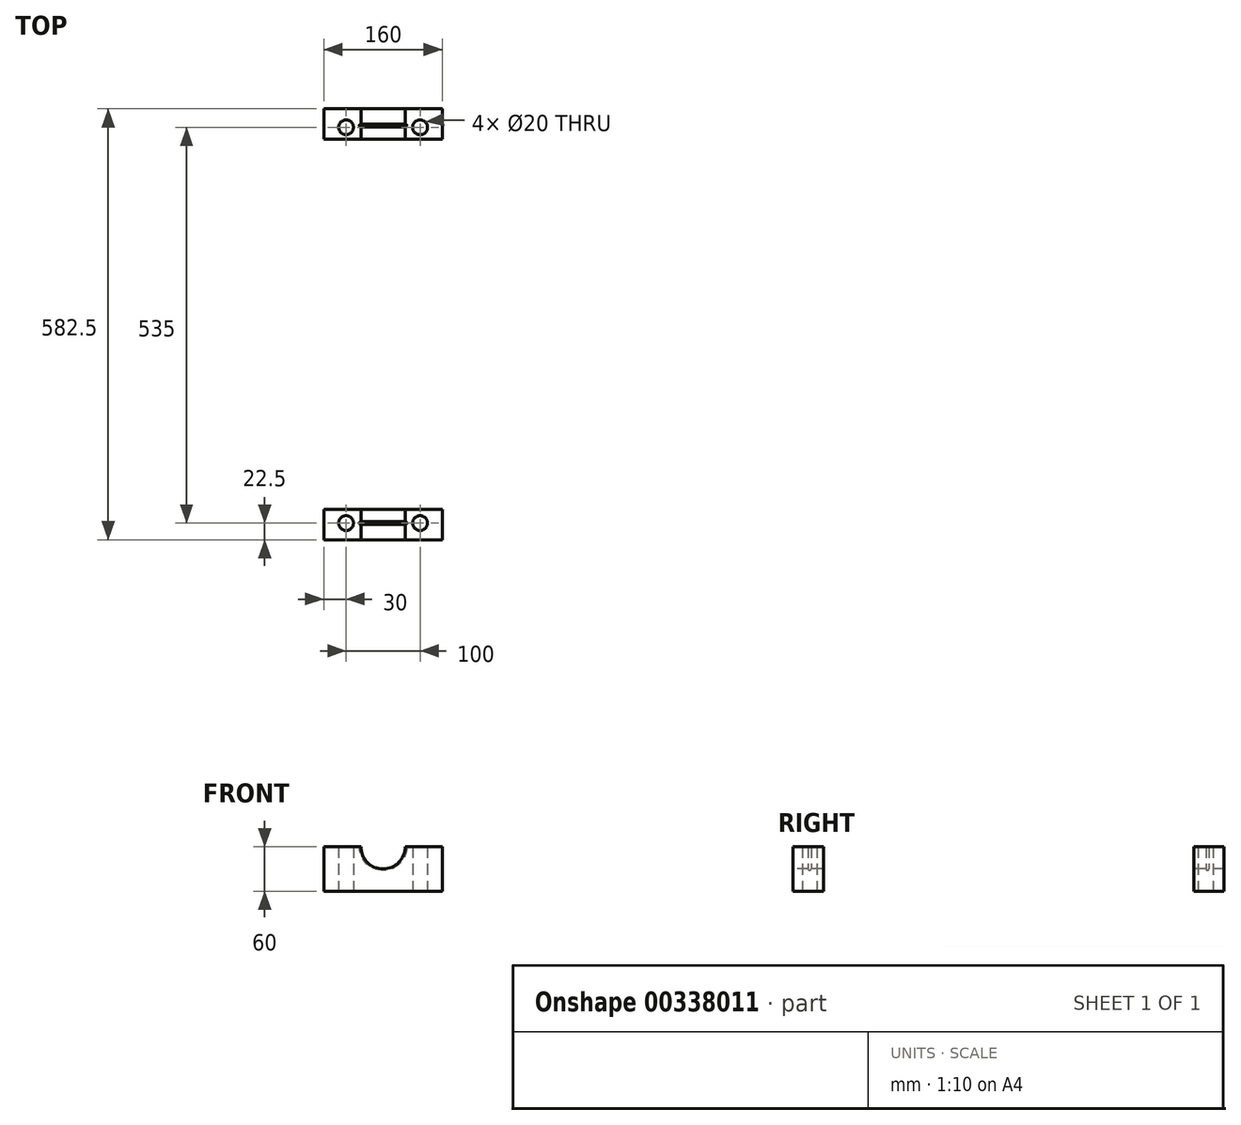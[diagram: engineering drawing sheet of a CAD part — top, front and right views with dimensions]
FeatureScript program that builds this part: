
annotation { "Feature Type Name" : "Feature", "Feature Type Description" : "" }
export const myFeature = defineFeature(function(context is Context, id is Id, definition is map)
    precondition{}
    {
        {
            var Q0;
            Q0=qCreatedBy(makeId("Top.planeOp"),FACE);
            var sketch = newSketch(context, id + "F0", { "sketchPlane" : qUnion([Q0])});
            skLineSegment(sketch, "E0", {"start": v(0, 267.5) * mm, "end": v(0, -267.5) * mm, "construction": true});
            skLineSegment(sketch, "E1.bottom", {"start": v(80, 287.5) * mm, "end": v(-80, 287.5) * mm});
            skLineSegment(sketch, "E1.top", {"start": v(80, 247.5) * mm, "end": v(-80, 247.5) * mm});
            skLineSegment(sketch, "E1.left", {"start": v(80, 287.5) * mm, "end": v(80, 247.5) * mm});
            skLineSegment(sketch, "E1.right", {"start": v(-80, 287.5) * mm, "end": v(-80, 247.5) * mm});
            skPoint(sketch, "E1.middle", {"position": v(0, 267.5) * mm});
            skLineSegment(sketch, "E2.bottom", {"start": v(80, -290) * mm, "end": v(-80, -290) * mm});
            skLineSegment(sketch, "E2.top", {"start": v(80, -245) * mm, "end": v(-80, -245) * mm});
            skLineSegment(sketch, "E2.left", {"start": v(80, -290) * mm, "end": v(80, -245) * mm});
            skLineSegment(sketch, "E2.right", {"start": v(-80, -290) * mm, "end": v(-80, -245) * mm});
            skPoint(sketch, "E2.middle", {"position": v(0, -267.5) * mm});
            skLineSegment(sketch, "E3", {"start": v(-80, 267.5) * mm, "end": v(80, 267.5) * mm, "construction": true});
            skLineSegment(sketch, "E4", {"start": v(-80, -267.5) * mm, "end": v(80, -267.5) * mm, "construction": true});
            skCircle(sketch, "E5", {"center": v(50, 267.5) * mm, "radius": 10 * mm});
            skLineSegment(sketch, "E6", {"start": v(-57.63, 0) * mm, "end": v(57.6, 0) * mm, "construction": true});
            skCircle(sketch, "E7.MirrorC", {"center": v(-50, 267.5) * mm, "radius": 10 * mm});
            skCircle(sketch, "E8.MirrorC", {"center": v(50, -267.5) * mm, "radius": 10 * mm});
            skCircle(sketch, "E9.MirrorC", {"center": v(-50, -267.5) * mm, "radius": 10 * mm});
            skSolve(sketch);
        }
        {
            var Q0;
            Q0 = qSketchRegion(id + "F0", true);
            extrude(context, id + "F1", {"entities" : qUnion([Q0]), "depth" : 60 * mm, "symmetric" : true});
        }
        {
            var Q0;
            Q0=makeQuery(id+"F1.opExtrude","SWEPT_FACE",FACE,{"disambiguationData":[OSD([sQuery(id+"F0.wireOp",EDGE,"E2.bottom")])]});
            var sketch = newSketch(context, id + "F2", { "sketchPlane" : qUnion([Q0])});
            skCircle(sketch, "E10", {"center": v(0, 30) * mm, "radius": 30 * mm});
            skSolve(sketch);
        }
        {
            var Q0;
            {var subQ0=sQuery(id+"F2.wireOp",EDGE,"E10");var subQ1=makeQuery(id+"F1.opExtrude","CAP_EDGE",EDGE,{"disambiguationData":[OSD([sQuery(id+"F0.wireOp",EDGE,"E2.bottom")])],"isStart":false});var subQ2=makeQuery(id+"F2.imprint","INTERSECT",VERTEX,{"disambiguationData":[OD(0.0)],"derivedFrom":[subQ1,subQ0]});Q0=makeQuery(id+"F2.imprint","IMPRINT",FACE,{"disambiguationData":[TD([[makeQuery(id+"F2.imprint","IMPRINT",EDGE,{"disambiguationData":[TD([[subQ2,1.0]])],"derivedFrom":subQ0}),1.0]])]});}
            var Q1;
            {var subQ0=sQuery(id+"F2.wireOp",EDGE,"E10");var subQ1=makeQuery(id+"F1.opExtrude","CAP_EDGE",EDGE,{"disambiguationData":[OSD([sQuery(id+"F0.wireOp",EDGE,"E2.bottom")])],"isStart":false});var subQ2=makeQuery(id+"F2.imprint","INTERSECT",VERTEX,{"disambiguationData":[OD(0.0)],"derivedFrom":[subQ1,subQ0]});Q1=makeQuery(id+"F2.imprint","IMPRINT",FACE,{"disambiguationData":[TD([[makeQuery(id+"F2.imprint","IMPRINT",EDGE,{"disambiguationData":[TD([[subQ2,-1.0]])],"derivedFrom":subQ0}),1.0]])]});}
            var Q2;
            Q2=makeQuery(id+"F1.opExtrude","SWEPT_FACE",FACE,{"disambiguationData":[OSD([sQuery(id+"F0.wireOp",EDGE,"E1.bottom")])]});
            extrude(context, id + "F3", {"entities" : qUnion([Q0, Q1]), "operationType" : NewBodyOperationType.REMOVE, "endBound" : BoundingType.THROUGH_ALL, "oppositeDirection" : true, "endBoundEntityFace" : qUnion([Q2]), "depth" : 535 * mm});
        }
        {
            var Q0;
            Q0=makeQuery(id+"F1.opExtrude","CAP_FACE",FACE,{"disambiguationData":[OSD([sQuery(id+"F0.wireOp",EDGE,"E2.bottom"),sQuery(id+"F0.wireOp",EDGE,"E2.top"),sQuery(id+"F0.wireOp",EDGE,"E2.left"),sQuery(id+"F0.wireOp",EDGE,"E2.right"),sQuery(id+"F0.wireOp",EDGE,"E8.MirrorC"),sQuery(id+"F0.wireOp",EDGE,"E9.MirrorC")])],"isStart":false});
            var sketch = newSketch(context, id + "F4", { "sketchPlane" : qUnion([Q0])});
            skCircle(sketch, "E11", {"center": v(30, 270) * mm, "radius": 2 * mm});
            skCircle(sketch, "E12", {"center": v(30, -267.5) * mm, "radius": 2 * mm});
            skLineSegment(sketch, "E13", {"start": v(0, -268.36) * mm, "end": v(0, 267.44) * mm, "construction": true});
            skSolve(sketch);
        }
        {
            var Q0;
            Q0 = qSketchRegion(id + "F4", true);
            var Q1;
            Q1=sQuery(id+"F4.wireOp",EDGE,"E13");
            revolve(context, id + "F5", {"operationType" : NewBodyOperationType.REMOVE, "entities" : qUnion([Q0]), "axis" : qUnion([Q1]), "revolveType" : RevolveType.FULL, "oppositeDirection" : true});
        }
        {
            var Q0;
            Q0=makeQuery(id+"F1.opExtrude","SWEPT_FACE",FACE,{"disambiguationData":[OSD([sQuery(id+"F0.wireOp",EDGE,"E1.bottom")])]});
            extrude(context, id + "F6", {"entities" : qUnion([Q0]), "operationType" : NewBodyOperationType.ADD, "depth" : 5 * mm});
        }
        {
            var Q0;
            Q0=makeQuery(id+"F1.opExtrude","SWEPT_FACE",FACE,{"disambiguationData":[OSD([sQuery(id+"F0.wireOp",EDGE,"E2.top")])]});
            extrude(context, id + "F7", {"entities" : qUnion([Q0]), "operationType" : NewBodyOperationType.REMOVE, "oppositeDirection" : true, "depth" : 4 * mm});
        }
        {
            var Q0;
            Q0=makeQuery(id+"F1.opExtrude","SWEPT_FACE",FACE,{"disambiguationData":[OSD([sQuery(id+"F0.wireOp",EDGE,"E1.top")])]});
            extrude(context, id + "F8", {"entities" : qUnion([Q0]), "operationType" : NewBodyOperationType.REMOVE, "oppositeDirection" : true, "depth" : 4 * mm});
        }
    });
